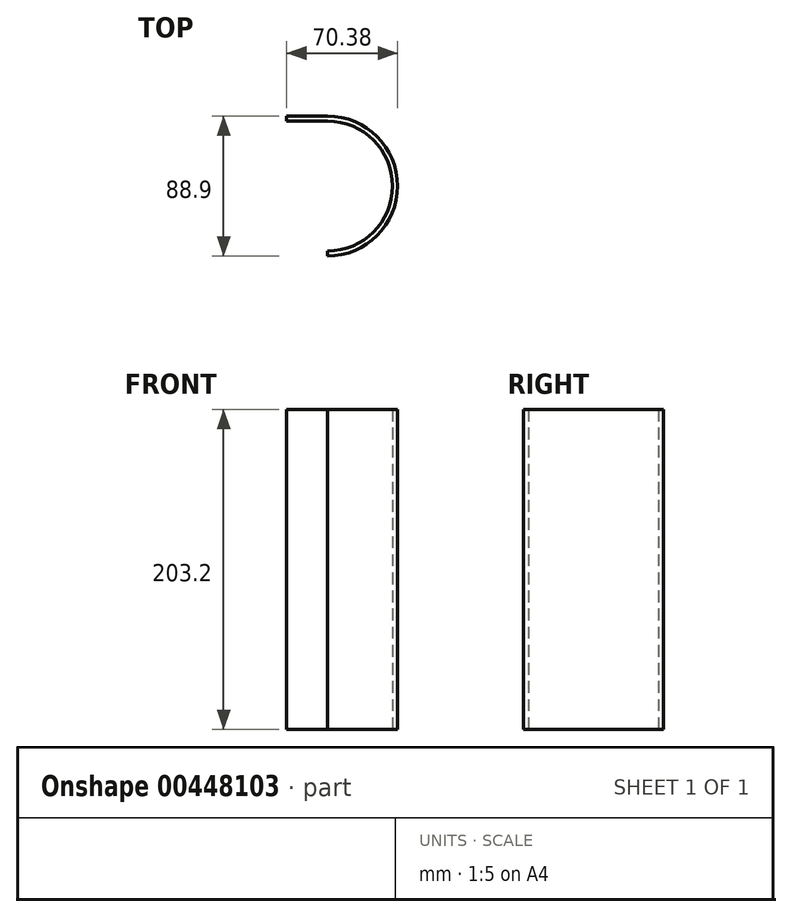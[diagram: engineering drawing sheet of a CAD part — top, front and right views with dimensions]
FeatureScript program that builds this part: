
annotation { "Feature Type Name" : "Feature", "Feature Type Description" : "" }
export const myFeature = defineFeature(function(context is Context, id is Id, definition is map)
    precondition{}
    {
        {
            var Q0;
            Q0=qCreatedBy(makeId("Top.planeOp"),FACE);
            var sketch = newSketch(context, id + "F0", { "sketchPlane" : qUnion([Q0])});
            skPoint(sketch, "E0.orphan", {"position": v(-0.17, 102.08) * mm});
            skArc(sketch, "E1.MirrorCS", {"start": v(93.74, 15.35) * mm, "mid": v(135.02, -25.92) * mm, "end": v(93.74, -67.2) * mm});
            skLineSegment(sketch, "E2.MirrorCS", {"start": v(67.81, 18.53) * mm, "end": v(93.74, 18.53) * mm});
            skArc(sketch, "E3", {"start": v(93.74, -70.37) * mm, "mid": v(138.2, -25.92) * mm, "end": v(93.74, 18.53) * mm});
            skLineSegment(sketch, "E4", {"start": v(67.81, 18.53) * mm, "end": v(67.81, 15.35) * mm});
            skLineSegment(sketch, "E5", {"start": v(93.74, 15.35) * mm, "end": v(67.81, 15.35) * mm});
            skLineSegment(sketch, "E6", {"start": v(93.74, -67.2) * mm, "end": v(93.74, -70.37) * mm});
            skSolve(sketch);
        }
        {
            var Q0;
            Q0 = qSketchRegion(id + "F0", true);
            extrude(context, id + "F1", {"entities" : qUnion([Q0]), "depth" : 203.2 * mm});
        }
    });
